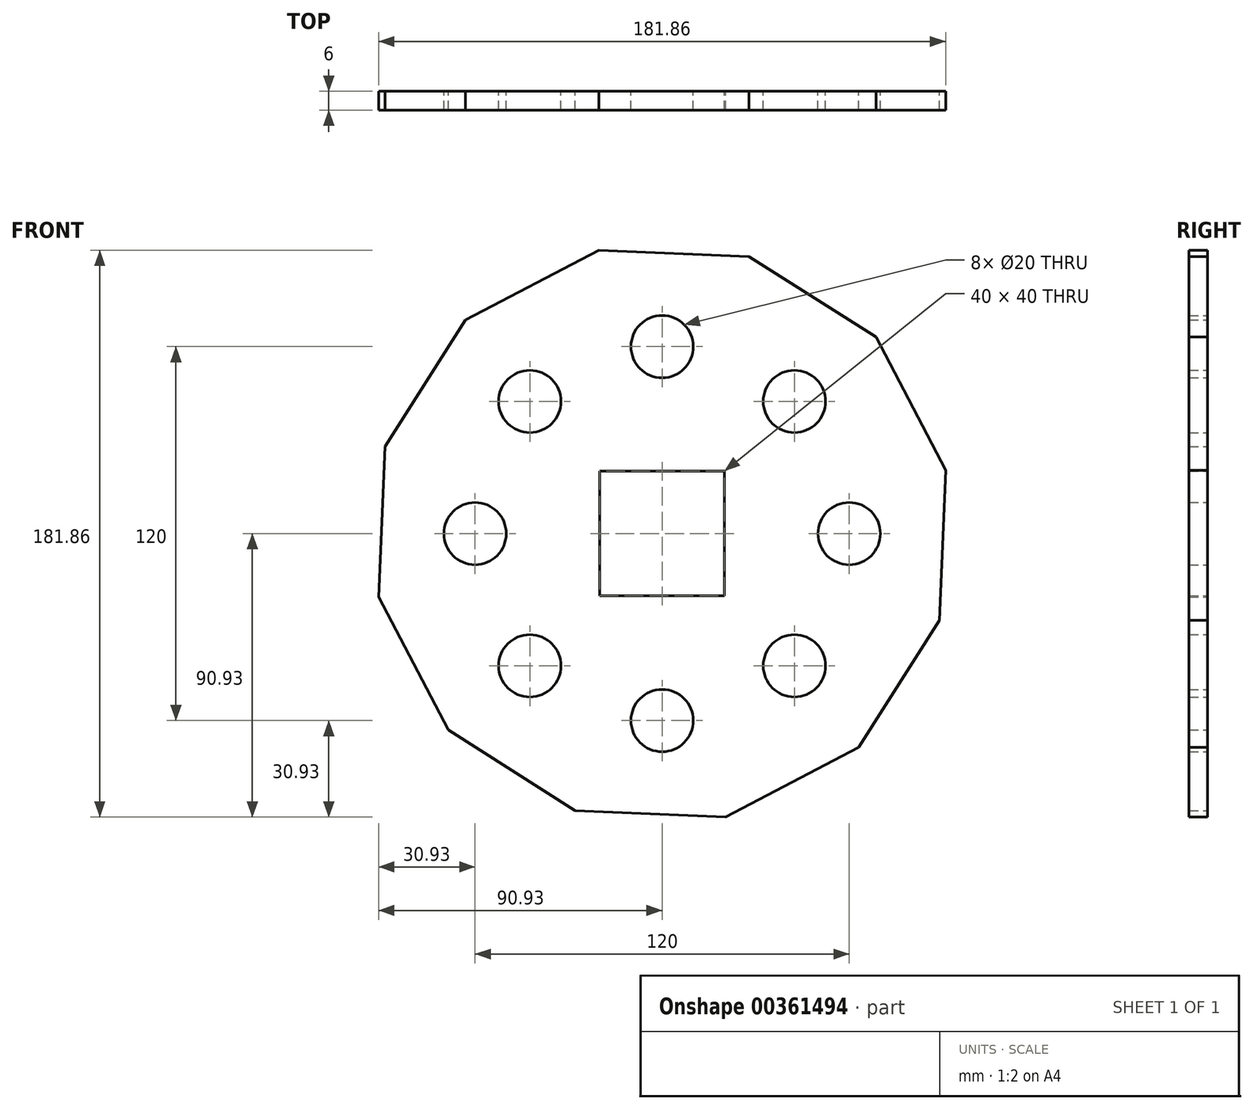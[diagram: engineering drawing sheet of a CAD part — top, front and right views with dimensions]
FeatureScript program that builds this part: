
annotation { "Feature Type Name" : "Feature", "Feature Type Description" : "" }
export const myFeature = defineFeature(function(context is Context, id is Id, definition is map)
    precondition{}
    {
        {
            var Q0;
            Q0=qCreatedBy(makeId("Front.planeOp"),FACE);
            var sketch = newSketch(context, id + "F0", { "sketchPlane" : qUnion([Q0])});
            skCircle(sketch, "E0.cCircle", {"center": v(0, 0) * mm, "radius": 90 * mm, "construction": true});
            skLineSegment(sketch, "E0.0", {"start": v(63.06, -68.6) * mm, "end": v(20.3, -90.93) * mm});
            skLineSegment(sketch, "E0.1", {"start": v(20.3, -90.93) * mm, "end": v(-27.88, -88.9) * mm});
            skLineSegment(sketch, "E0.2", {"start": v(-27.88, -88.9) * mm, "end": v(-68.6, -63.06) * mm});
            skLineSegment(sketch, "E0.3", {"start": v(-68.6, -63.06) * mm, "end": v(-90.93, -20.3) * mm});
            skLineSegment(sketch, "E0.4", {"start": v(-90.93, -20.3) * mm, "end": v(-88.9, 27.88) * mm});
            skLineSegment(sketch, "E0.5", {"start": v(-88.9, 27.88) * mm, "end": v(-63.06, 68.6) * mm});
            skLineSegment(sketch, "E0.6", {"start": v(-63.06, 68.6) * mm, "end": v(-20.3, 90.93) * mm});
            skLineSegment(sketch, "E0.7", {"start": v(-20.3, 90.93) * mm, "end": v(27.88, 88.9) * mm});
            skLineSegment(sketch, "E0.8", {"start": v(27.88, 88.9) * mm, "end": v(68.6, 63.06) * mm});
            skLineSegment(sketch, "E0.9", {"start": v(68.6, 63.06) * mm, "end": v(90.93, 20.3) * mm});
            skLineSegment(sketch, "E0.10", {"start": v(90.93, 20.3) * mm, "end": v(88.9, -27.88) * mm});
            skLineSegment(sketch, "E0.11", {"start": v(88.9, -27.88) * mm, "end": v(63.06, -68.6) * mm});
            skPoint(sketch, "E0.0.midPoint", {"position": v(41.68, -79.77) * mm});
            skCircle(sketch, "E1", {"center": v(0, 0) * mm, "radius": 60 * mm, "construction": true});
            skLineSegment(sketch, "E2.bottom", {"start": v(20, -20) * mm, "end": v(-20, -20) * mm});
            skLineSegment(sketch, "E2.top", {"start": v(20, 20) * mm, "end": v(-20, 20) * mm});
            skLineSegment(sketch, "E2.left", {"start": v(20, -20) * mm, "end": v(20, 20) * mm});
            skLineSegment(sketch, "E2.right", {"start": v(-20, -20) * mm, "end": v(-20, 20) * mm});
            skCircle(sketch, "E3", {"center": v(60, 0) * mm, "radius": 10 * mm});
            skCircle(sketch, "E4.1.1", {"center": v(42.43, 42.43) * mm, "radius": 10 * mm});
            skCircle(sketch, "E4.2.1", {"center": v(0, 60) * mm, "radius": 10 * mm});
            skCircle(sketch, "E4.3.1", {"center": v(-42.43, 42.43) * mm, "radius": 10 * mm});
            skCircle(sketch, "E4.4.1", {"center": v(-60, 0) * mm, "radius": 10 * mm});
            skCircle(sketch, "E4.5.1", {"center": v(-42.43, -42.43) * mm, "radius": 10 * mm});
            skCircle(sketch, "E4.6.1", {"center": v(0, -60) * mm, "radius": 10 * mm});
            skCircle(sketch, "E4.7.1", {"center": v(42.43, -42.43) * mm, "radius": 10 * mm});
            skSolve(sketch);
        }
        {
            var Q0;
            Q0 = qSketchRegion(id + "F0", true);
            extrude(context, id + "F1", {"entities" : qUnion([Q0]), "depth" : 6 * mm});
        }
    });
